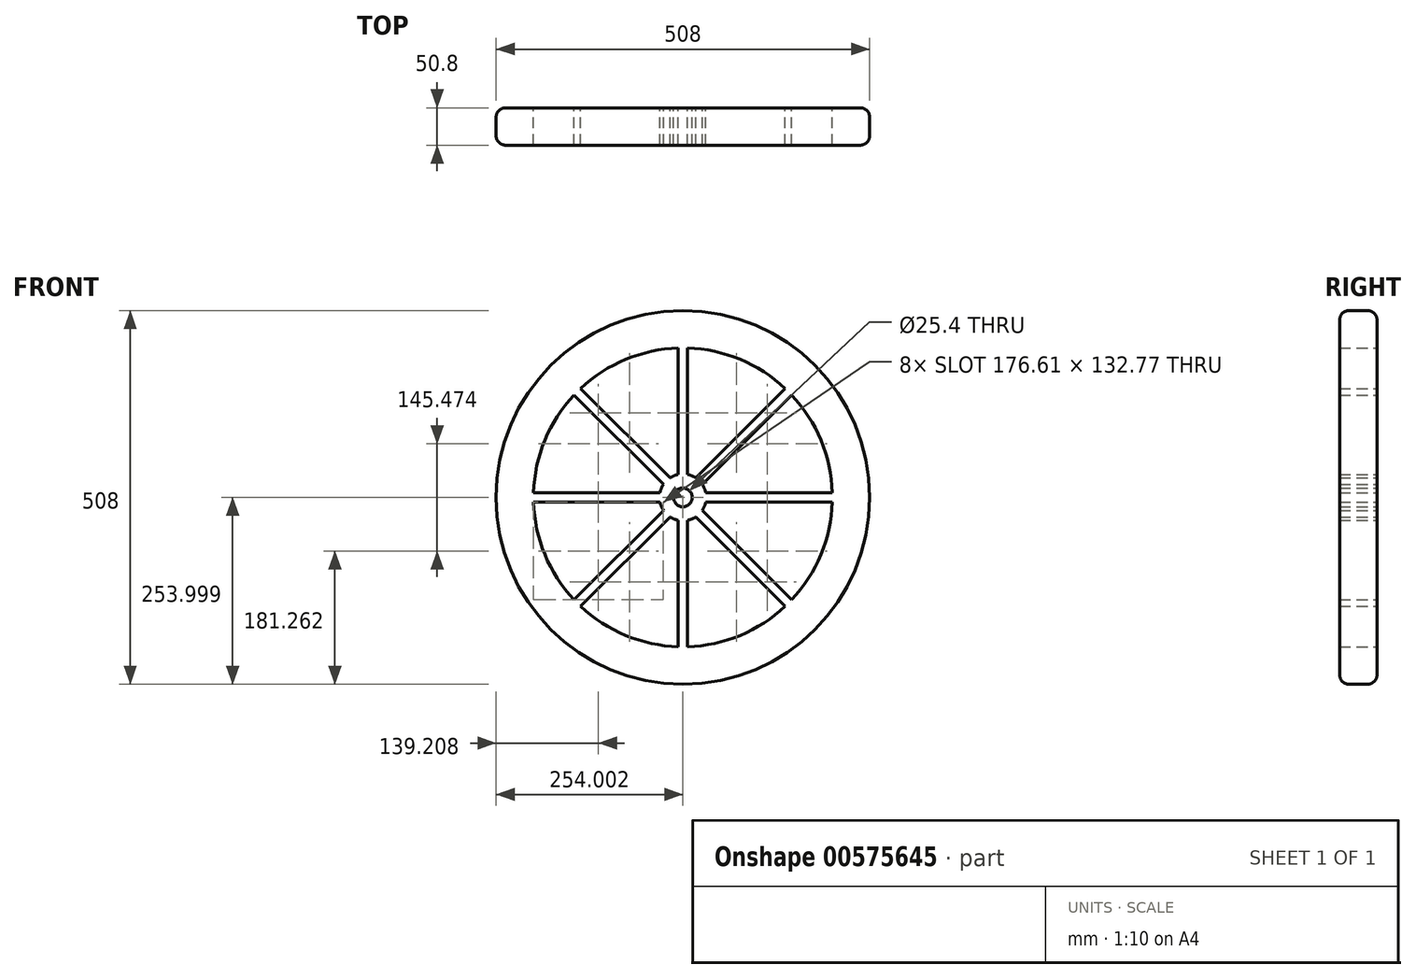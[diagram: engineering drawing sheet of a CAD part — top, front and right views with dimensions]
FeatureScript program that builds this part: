
annotation { "Feature Type Name" : "Feature", "Feature Type Description" : "" }
export const myFeature = defineFeature(function(context is Context, id is Id, definition is map)
    precondition{}
    {
        {
            var Q0;
            Q0=qCreatedBy(makeId("Front.planeOp"),FACE);
            var sketch = newSketch(context, id + "F0", { "sketchPlane" : qUnion([Q0])});
            skCircle(sketch, "E0", {"center": v(-79.28, 3.37) * mm, "radius": 254 * mm});
            skCircle(sketch, "E1", {"center": v(-79.28, 3.37) * mm, "radius": 12.7 * mm});
            skArc(sketch, "E2.0", {"start": v(-282.38, -2.98) * mm, "mid": v(-267.01, -74.4) * mm, "end": v(-227.38, -135.75) * mm});
            skLineSegment(sketch, "E3.0", {"start": v(-72.93, 34.48) * mm, "end": v(-72.93, 206.47) * mm});
            skLineSegment(sketch, "E4.0", {"start": v(-85.63, 34.48) * mm, "end": v(-85.63, 206.47) * mm});
            skLineSegment(sketch, "E5.1.0", {"start": v(-96.78, 29.86) * mm, "end": v(-218.4, 151.47) * mm});
            skLineSegment(sketch, "E5.1.1", {"start": v(-105.76, 20.88) * mm, "end": v(-227.38, 142.5) * mm});
            skLineSegment(sketch, "E5.2.0", {"start": v(-110.39, 9.72) * mm, "end": v(-282.38, 9.72) * mm});
            skLineSegment(sketch, "E5.2.1", {"start": v(-110.39, -2.98) * mm, "end": v(-282.38, -2.98) * mm});
            skLineSegment(sketch, "E5.3.0", {"start": v(-105.76, -14.14) * mm, "end": v(-227.38, -135.75) * mm});
            skLineSegment(sketch, "E5.3.1", {"start": v(-96.78, -23.12) * mm, "end": v(-218.4, -144.74) * mm});
            skLineSegment(sketch, "E5.4.0", {"start": v(-85.63, -27.74) * mm, "end": v(-85.63, -199.73) * mm});
            skLineSegment(sketch, "E5.4.1", {"start": v(-72.93, -27.74) * mm, "end": v(-72.93, -199.73) * mm});
            skLineSegment(sketch, "E5.5.0", {"start": v(-61.77, -23.12) * mm, "end": v(59.85, -144.74) * mm});
            skLineSegment(sketch, "E5.5.1", {"start": v(-52.8, -14.14) * mm, "end": v(68.83, -135.75) * mm});
            skLineSegment(sketch, "E5.6.0", {"start": v(-48.17, -2.98) * mm, "end": v(123.82, -2.98) * mm});
            skLineSegment(sketch, "E5.6.1", {"start": v(-48.17, 9.72) * mm, "end": v(123.82, 9.72) * mm});
            skLineSegment(sketch, "E5.7.0", {"start": v(-52.8, 20.88) * mm, "end": v(68.83, 142.5) * mm});
            skLineSegment(sketch, "E5.7.1", {"start": v(-61.77, 29.86) * mm, "end": v(59.85, 151.47) * mm});
            skPoint(sketch, "E6.orphan", {"position": v(-91.55, 0.08) * mm});
            skPoint(sketch, "E7.orphan", {"position": v(-90.28, -2.98) * mm});
            skPoint(sketch, "E8.orphan", {"position": v(-85.63, -7.63) * mm});
            skPoint(sketch, "E9.orphan", {"position": v(-82.56, -8.9) * mm});
            skPoint(sketch, "E10.orphan", {"position": v(-76, -8.9) * mm});
            skPoint(sketch, "E11.orphan", {"position": v(-72.93, -7.63) * mm});
            skPoint(sketch, "E12.orphan", {"position": v(-67.01, 0.08) * mm});
            skPoint(sketch, "E13.orphan", {"position": v(-68.28, -2.98) * mm});
            skPoint(sketch, "E14.orphan", {"position": v(-76, 15.64) * mm});
            skPoint(sketch, "E15.orphan", {"position": v(-72.93, 14.37) * mm});
            skPoint(sketch, "E16.orphan", {"position": v(-68.28, 9.72) * mm});
            skPoint(sketch, "E17.orphan", {"position": v(-67.01, 6.66) * mm});
            skPoint(sketch, "E18.orphan", {"position": v(-85.63, 14.37) * mm});
            skPoint(sketch, "E19.orphan", {"position": v(-82.56, 15.64) * mm});
            skPoint(sketch, "E20.orphan", {"position": v(-91.55, 6.66) * mm});
            skPoint(sketch, "E21.orphan", {"position": v(-90.28, 9.72) * mm});
            skArc(sketch, "E22.trimOffspring", {"start": v(-227.38, 142.5) * mm, "mid": v(-267.01, 81.13) * mm, "end": v(-282.38, 9.72) * mm});
            skArc(sketch, "E23.trimOffspring", {"start": v(-85.63, 206.47) * mm, "mid": v(-157.04, 191.1) * mm, "end": v(-218.4, 151.47) * mm});
            skArc(sketch, "E24.trimOffspring", {"start": v(59.85, 151.47) * mm, "mid": v(-1.52, 191.1) * mm, "end": v(-72.93, 206.47) * mm});
            skArc(sketch, "E25.trimOffspring", {"start": v(123.82, 9.72) * mm, "mid": v(108.45, 81.13) * mm, "end": v(68.83, 142.5) * mm});
            skArc(sketch, "E26.trimOffspring", {"start": v(-218.4, -144.74) * mm, "mid": v(-157.04, -184.36) * mm, "end": v(-85.63, -199.73) * mm});
            skArc(sketch, "E27.trimOffspring", {"start": v(-72.93, -199.73) * mm, "mid": v(-1.52, -184.36) * mm, "end": v(59.85, -144.74) * mm});
            skArc(sketch, "E28.trimOffspring", {"start": v(68.83, -135.75) * mm, "mid": v(108.45, -74.4) * mm, "end": v(123.82, -2.98) * mm});
            skArc(sketch, "E29", {"start": v(-61.77, 29.86) * mm, "mid": v(-67.13, 32.7) * mm, "end": v(-72.93, 34.48) * mm});
            skArc(sketch, "E30.trimOffspring", {"start": v(-85.63, 34.48) * mm, "mid": v(-91.43, 32.7) * mm, "end": v(-96.78, 29.86) * mm});
            skArc(sketch, "E31.trimOffspring", {"start": v(-105.76, 20.88) * mm, "mid": v(-108.61, 15.52) * mm, "end": v(-110.39, 9.72) * mm});
            skArc(sketch, "E32.trimOffspring", {"start": v(-110.39, -2.98) * mm, "mid": v(-108.61, -8.78) * mm, "end": v(-105.76, -14.14) * mm});
            skArc(sketch, "E33.trimOffspring", {"start": v(-96.78, -23.12) * mm, "mid": v(-91.43, -25.96) * mm, "end": v(-85.63, -27.74) * mm});
            skArc(sketch, "E34.trimOffspring", {"start": v(-72.93, -27.74) * mm, "mid": v(-67.13, -25.96) * mm, "end": v(-61.77, -23.12) * mm});
            skArc(sketch, "E35.trimOffspring", {"start": v(-52.8, -14.14) * mm, "mid": v(-49.94, -8.78) * mm, "end": v(-48.17, -2.98) * mm});
            skArc(sketch, "E36.trimOffspring", {"start": v(-48.17, 9.72) * mm, "mid": v(-49.94, 15.52) * mm, "end": v(-52.8, 20.88) * mm});
            skLineSegment(sketch, "E37.trimOffspring", {"start": v(-254.34, 187.4) * mm, "end": v(-254.4, 187.46) * mm});
            skLineSegment(sketch, "E38.trimOffspring", {"start": v(-263.32, 178.43) * mm, "end": v(-263.37, 178.48) * mm});
            skLineSegment(sketch, "E39.trimOffspring", {"start": v(-85.63, 257.29) * mm, "end": v(-85.63, 257.37) * mm});
            skLineSegment(sketch, "E40.trimOffspring", {"start": v(-72.93, 257.29) * mm, "end": v(-72.93, 257.37) * mm});
            skLineSegment(sketch, "E41.trimOffspring", {"start": v(104.76, 178.43) * mm, "end": v(104.82, 178.48) * mm});
            skLineSegment(sketch, "E42.trimOffspring", {"start": v(95.78, 187.4) * mm, "end": v(95.84, 187.46) * mm});
            skLineSegment(sketch, "E43.trimOffspring", {"start": v(174.64, 9.72) * mm, "end": v(174.72, 9.72) * mm});
            skLineSegment(sketch, "E44.trimOffspring", {"start": v(174.64, -2.98) * mm, "end": v(174.72, -2.98) * mm});
            skLineSegment(sketch, "E45.trimOffspring", {"start": v(104.76, -171.7) * mm, "end": v(104.82, -171.75) * mm});
            skLineSegment(sketch, "E46.trimOffspring", {"start": v(95.78, -180.67) * mm, "end": v(95.84, -180.73) * mm});
            skLineSegment(sketch, "E47.trimOffspring", {"start": v(-72.93, -250.55) * mm, "end": v(-72.93, -250.63) * mm});
            skLineSegment(sketch, "E48.trimOffspring", {"start": v(-85.63, -250.55) * mm, "end": v(-85.63, -250.63) * mm});
            skLineSegment(sketch, "E49.trimOffspring", {"start": v(-254.34, -180.67) * mm, "end": v(-254.4, -180.73) * mm});
            skLineSegment(sketch, "E50.trimOffspring", {"start": v(-263.32, -171.7) * mm, "end": v(-263.37, -171.75) * mm});
            skLineSegment(sketch, "E51.trimOffspring", {"start": v(-333.2, -2.98) * mm, "end": v(-333.28, -2.98) * mm});
            skLineSegment(sketch, "E52.trimOffspring", {"start": v(-333.2, 9.72) * mm, "end": v(-333.28, 9.72) * mm});
            skSolve(sketch);
        }
        {
            var Q0;
            Q0=qSketchRegion(id+"F0",true);
            extrude(context, id + "F1", {"entities" : qUnion([Q0]), "depth" : 50.8 * mm, "offsetDistance" : 25.4 * mm});
        }
        {
            var Q0;
            Q0=makeQuery(id+"F1.opExtrude","CAP_EDGE",EDGE,{"disambiguationData":[OSD([sQuery(id+"F0.wireOp",EDGE,"E0")])],"isStart":false});
            var Q1;
            Q1=makeQuery(id+"F1.opExtrude","CAP_EDGE",EDGE,{"disambiguationData":[OSD([sQuery(id+"F0.wireOp",EDGE,"E0")])],"isStart":true});
            fillet(context, id + "F2", {"entities" : qUnion([Q0, Q1]), "radius" : 12.7 * mm, "tangentPropagation" : true, "allowEdgeOverflow" : false});
        }
    });
